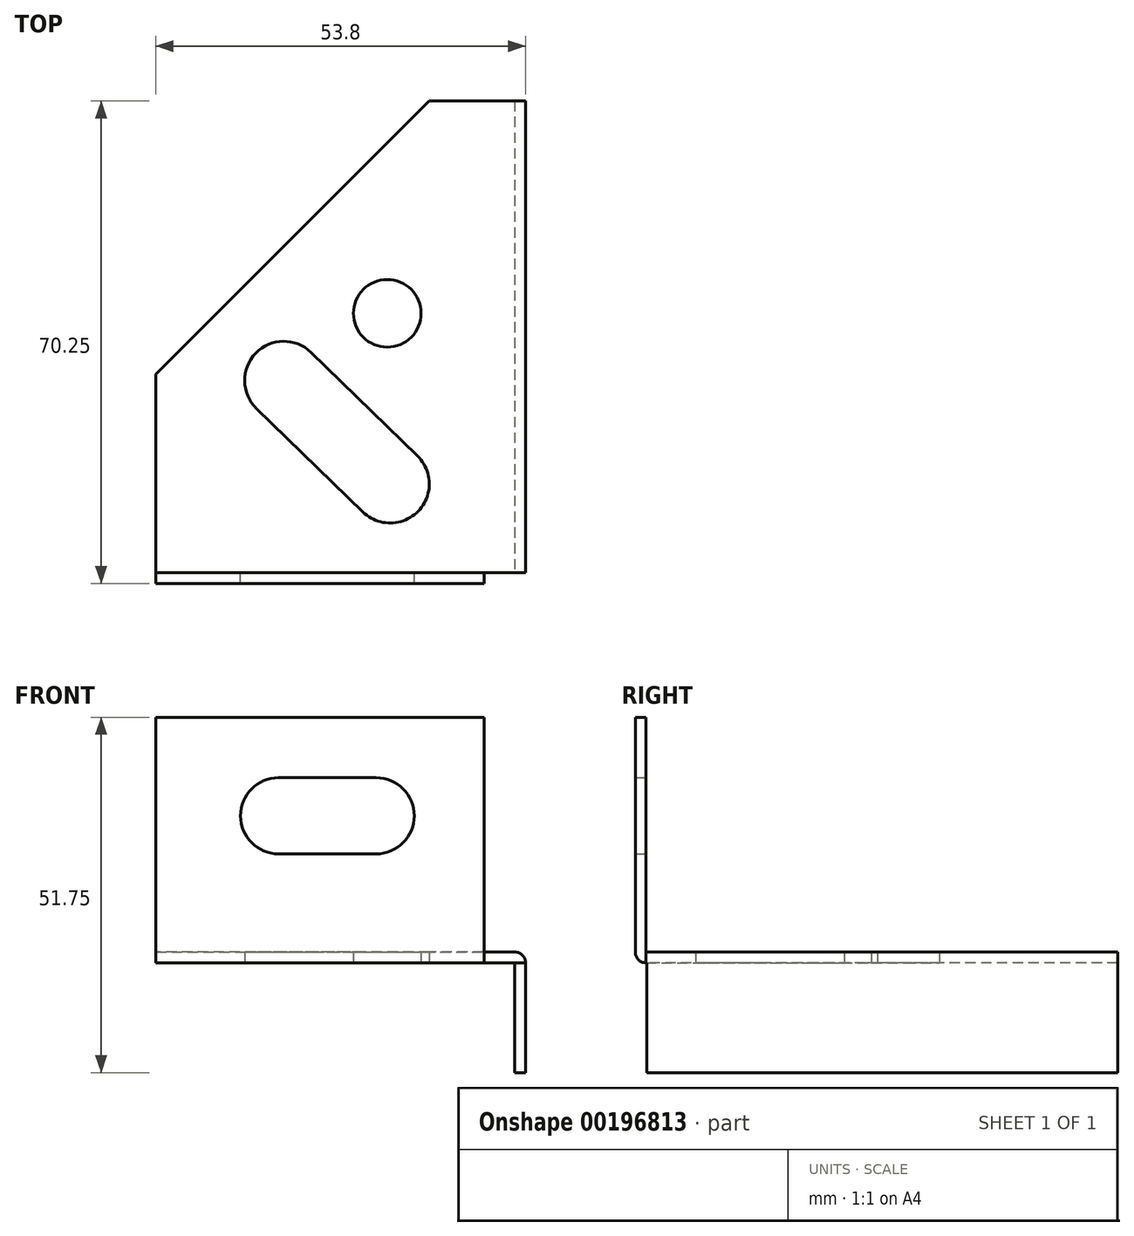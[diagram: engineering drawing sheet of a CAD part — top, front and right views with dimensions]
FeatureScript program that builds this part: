
annotation { "Feature Type Name" : "Feature", "Feature Type Description" : "" }
export const myFeature = defineFeature(function(context is Context, id is Id, definition is map)
    precondition{}
    {
        {
            var Q0;
            Q0=qCreatedBy(makeId("Top.planeOp"),FACE);
            var sketch = newSketch(context, id + "F0", { "sketchPlane" : qUnion([Q0])});
            skLineSegment(sketch, "E0", {"start": v(-51.36, -58.28) * mm, "end": v(2.44, -58.28) * mm});
            skLineSegment(sketch, "E1", {"start": v(2.44, -58.28) * mm, "end": v(2.44, -29.38) * mm});
            skLineSegment(sketch, "E2", {"start": v(-51.36, -58.28) * mm, "end": v(-51.36, 10.42) * mm});
            skLineSegment(sketch, "E3", {"start": v(-51.36, 10.42) * mm, "end": v(-37.36, 10.42) * mm});
            skLineSegment(sketch, "E4", {"start": v(-37.36, 10.42) * mm, "end": v(2.44, -29.38) * mm});
            skCircle(sketch, "E5", {"center": v(-31.23, -20.5) * mm, "radius": 4.92 * mm});
            skCircle(sketch, "E6", {"center": v(-31.66, -45.34) * mm, "radius": 5.7 * mm});
            skCircle(sketch, "E7", {"center": v(-16.17, -30.28) * mm, "radius": 5.7 * mm});
            skLineSegment(sketch, "E8", {"start": v(-20.15, -26.2) * mm, "end": v(-35.63, -41.25) * mm});
            skLineSegment(sketch, "E9", {"start": v(-27.68, -49.42) * mm, "end": v(-12.2, -34.36) * mm});
            skSolve(sketch);
        }
        {
            var Q0;
            Q0=makeQuery(id+"F0.imprint","IMPRINT",FACE,{"disambiguationData":[TD([[makeQuery(id+"F0.imprint","IMPRINT",EDGE,{"derivedFrom":sQuery(id+"F0.wireOp",EDGE,"E0")}),1.0]])]});
            extrude(context, id + "F1", {"entities" : qUnion([Q0]), "depth" : 1.55 * mm});
        }
        {
            var Q0;
            Q0=makeQuery(id+"F1.opExtrude","CAP_FACE",FACE,{"disambiguationData":[OSD([sQuery(id+"F0.wireOp",EDGE,"E0"),sQuery(id+"F0.wireOp",EDGE,"E1"),sQuery(id+"F0.wireOp",EDGE,"E2"),sQuery(id+"F0.wireOp",EDGE,"E3"),sQuery(id+"F0.wireOp",EDGE,"E4"),sQuery(id+"F0.wireOp",EDGE,"E5"),sQuery(id+"F0.wireOp",EDGE,"E6"),sQuery(id+"F0.wireOp",EDGE,"E7"),sQuery(id+"F0.wireOp",EDGE,"E8"),sQuery(id+"F0.wireOp",EDGE,"E9")])],"isStart":true});
            var sketch = newSketch(context, id + "F2", { "sketchPlane" : qUnion([Q0])});
            skLineSegment(sketch, "E10.bottom", {"start": v(-51.36, -10.42) * mm, "end": v(-49.8, -10.42) * mm});
            skLineSegment(sketch, "E10.top", {"start": v(-51.36, 58.18) * mm, "end": v(-49.8, 58.18) * mm});
            skLineSegment(sketch, "E10.left", {"start": v(-51.36, -10.42) * mm, "end": v(-51.36, 58.18) * mm});
            skLineSegment(sketch, "E10.right", {"start": v(-49.8, -10.42) * mm, "end": v(-49.8, 58.18) * mm});
            skSolve(sketch);
        }
        {
            var Q0;
            Q0=makeQuery(id+"F2.imprint","IMPRINT",FACE,{"disambiguationData":[TD([[makeQuery(id+"F2.imprint","IMPRINT",EDGE,{"derivedFrom":sQuery(id+"F2.wireOp",EDGE,"E10.bottom")}),1.0]])]});
            extrude(context, id + "F3", {"entities" : qUnion([Q0]), "operationType" : NewBodyOperationType.ADD, "depth" : 16 * mm});
        }
        {
            var Q0;
            Q0=makeQuery(id+"F1.opExtrude","CAP_FACE",FACE,{"disambiguationData":[OSD([sQuery(id+"F0.wireOp",EDGE,"E0"),sQuery(id+"F0.wireOp",EDGE,"E1"),sQuery(id+"F0.wireOp",EDGE,"E2"),sQuery(id+"F0.wireOp",EDGE,"E3"),sQuery(id+"F0.wireOp",EDGE,"E4"),sQuery(id+"F0.wireOp",EDGE,"E5"),sQuery(id+"F0.wireOp",EDGE,"E6"),sQuery(id+"F0.wireOp",EDGE,"E7"),sQuery(id+"F0.wireOp",EDGE,"E8"),sQuery(id+"F0.wireOp",EDGE,"E9")])],"isStart":false});
            var sketch = newSketch(context, id + "F4", { "sketchPlane" : qUnion([Q0])});
            skLineSegment(sketch, "E11.bottom", {"start": v(2.44, -58.28) * mm, "end": v(-45.36, -58.28) * mm});
            skLineSegment(sketch, "E11.top", {"start": v(2.44, -59.83) * mm, "end": v(-45.36, -59.83) * mm});
            skLineSegment(sketch, "E11.left", {"start": v(2.44, -58.28) * mm, "end": v(2.44, -59.83) * mm});
            skLineSegment(sketch, "E11.right", {"start": v(-45.36, -58.28) * mm, "end": v(-45.36, -59.83) * mm});
            skSolve(sketch);
        }
        {
            var Q0;
            Q0=makeQuery(id+"F4.imprint","IMPRINT",FACE,{"disambiguationData":[TD([[makeQuery(id+"F4.imprint","IMPRINT",EDGE,{"derivedFrom":sQuery(id+"F4.wireOp",EDGE,"E11.bottom")}),-1.0]])]});
            extrude(context, id + "F5", {"entities" : qUnion([Q0]), "operationType" : NewBodyOperationType.ADD, "oppositeDirection" : true, "depth" : 1.55 * mm});
        }
        {
            var Q0;
            Q0=makeQuery(id+"F5.boolean.opBoolean","MERGE",FACE,{"derivedFrom":[makeQuery(id+"F1.opExtrude","CAP_FACE",FACE,{"disambiguationData":[OSD([sQuery(id+"F0.wireOp",EDGE,"E0"),sQuery(id+"F0.wireOp",EDGE,"E1"),sQuery(id+"F0.wireOp",EDGE,"E2"),sQuery(id+"F0.wireOp",EDGE,"E3"),sQuery(id+"F0.wireOp",EDGE,"E4"),sQuery(id+"F0.wireOp",EDGE,"E5"),sQuery(id+"F0.wireOp",EDGE,"E6"),sQuery(id+"F0.wireOp",EDGE,"E7"),sQuery(id+"F0.wireOp",EDGE,"E8"),sQuery(id+"F0.wireOp",EDGE,"E9")])],"isStart":false}),makeQuery(id+"F5.opExtrude","CAP_FACE",FACE,{"disambiguationData":[OSD([sQuery(id+"F4.wireOp",EDGE,"E11.bottom"),sQuery(id+"F4.wireOp",EDGE,"E11.top"),sQuery(id+"F4.wireOp",EDGE,"E11.left"),sQuery(id+"F4.wireOp",EDGE,"E11.right")])],"isStart":true})]});
            var sketch = newSketch(context, id + "F6", { "sketchPlane" : qUnion([Q0])});
            skLineSegment(sketch, "E12.bottom", {"start": v(2.44, -59.83) * mm, "end": v(-45.36, -59.83) * mm});
            skLineSegment(sketch, "E12.top", {"start": v(2.44, -58.28) * mm, "end": v(-45.36, -58.28) * mm});
            skLineSegment(sketch, "E12.left", {"start": v(2.44, -59.83) * mm, "end": v(2.44, -58.28) * mm});
            skLineSegment(sketch, "E12.right", {"start": v(-45.36, -59.83) * mm, "end": v(-45.36, -58.28) * mm});
            skSolve(sketch);
        }
        {
            var Q0;
            Q0=makeQuery(id+"F6.imprint","IMPRINT",FACE,{"disambiguationData":[TD([[makeQuery(id+"F6.imprint","IMPRINT",EDGE,{"derivedFrom":sQuery(id+"F6.wireOp",EDGE,"E12.bottom")}),-1.0]])]});
            extrude(context, id + "F7", {"entities" : qUnion([Q0]), "operationType" : NewBodyOperationType.ADD, "depth" : 34.2 * mm});
        }
        {
            var Q0;
            Q0=makeQuery(id+"F5.opExtrude","CAP_EDGE",EDGE,{"disambiguationData":[OSD([sQuery(id+"F4.wireOp",EDGE,"E11.top")])],"isStart":false});
            var Q1;
            Q1=makeQuery(id+"F1.opExtrude","CAP_EDGE",EDGE,{"disambiguationData":[OSD([sQuery(id+"F0.wireOp",EDGE,"E2")])],"isStart":false});
            fillet(context, id + "F8", {"entities" : qUnion([Q0, Q1]), "radius" : 1.5 * mm, "tangentPropagation" : true, "allowEdgeOverflow" : false});
        }
        {
            var Q0;
            Q0=makeQuery(id+"F1.opExtrude","SWEPT_BODY",BODY,{"disambiguationData":[OSD([sQuery(id+"F0.wireOp",EDGE,"E0"),sQuery(id+"F0.wireOp",EDGE,"E1"),sQuery(id+"F0.wireOp",EDGE,"E2"),sQuery(id+"F0.wireOp",EDGE,"E3"),sQuery(id+"F0.wireOp",EDGE,"E4"),sQuery(id+"F0.wireOp",EDGE,"E5"),sQuery(id+"F0.wireOp",EDGE,"E6"),sQuery(id+"F0.wireOp",EDGE,"E7"),sQuery(id+"F0.wireOp",EDGE,"E8"),sQuery(id+"F0.wireOp",EDGE,"E9")])]});
            var Q1;
            Q1=qCreatedBy(makeId("Right.planeOp"),FACE);
            mirror(context, id + "F9", {"entities" : qUnion([Q0]), "mirrorPlane" : qUnion([Q1])});
        }
        {
            var Q0;
            Q0=makeQuery(id+"F1.opExtrude","SWEPT_BODY",BODY,{"disambiguationData":[OSD([sQuery(id+"F0.wireOp",EDGE,"E0"),sQuery(id+"F0.wireOp",EDGE,"E1"),sQuery(id+"F0.wireOp",EDGE,"E2"),sQuery(id+"F0.wireOp",EDGE,"E3"),sQuery(id+"F0.wireOp",EDGE,"E4"),sQuery(id+"F0.wireOp",EDGE,"E5"),sQuery(id+"F0.wireOp",EDGE,"E6"),sQuery(id+"F0.wireOp",EDGE,"E7"),sQuery(id+"F0.wireOp",EDGE,"E8"),sQuery(id+"F0.wireOp",EDGE,"E9")])]});
            deleteBodies(context, id + "F10", {"entities" : qUnion([Q0])});
        }
        {
            var Q0;
            Q0=makeQuery(id+"F9.opPattern","COPY",FACE,{"derivedFrom":makeQuery(id+"F7.opExtrude","SWEPT_FACE",FACE,{"disambiguationData":[OSD([sQuery(id+"F6.wireOp",EDGE,"E12.top")])]}),"instanceName":"1"});
            var sketch = newSketch(context, id + "F11", { "sketchPlane" : qUnion([Q0])});
            skCircle(sketch, "E13", {"center": v(-29.6, 21.4) * mm, "radius": 5.55 * mm});
            skCircle(sketch, "E14", {"center": v(-15.4, 21.4) * mm, "radius": 5.55 * mm});
            skLineSegment(sketch, "E15", {"start": v(-29.6, 26.95) * mm, "end": v(-15.4, 26.95) * mm});
            skLineSegment(sketch, "E16", {"start": v(-29.6, 15.85) * mm, "end": v(-15.4, 15.85) * mm});
            skSolve(sketch);
        }
        {
            var Q0;
            {var subQ0=sQuery(id+"F11.wireOp",EDGE,"E13");var subQ1=makeQuery(id+"F11.imprint","INTERSECT",VERTEX,{"derivedFrom":[subQ0,sQuery(id+"F11.wireOp",EDGE,"E15")]});Q0=makeQuery(id+"F11.imprint","IMPRINT",FACE,{"disambiguationData":[TD([[makeQuery(id+"F11.imprint","IMPRINT",EDGE,{"disambiguationData":[TD([[subQ1,-1.0]])],"derivedFrom":subQ0}),1.0]])]});}
            var Q1;
            {var subQ0=sQuery(id+"F11.wireOp",EDGE,"E15");Q1=makeQuery(id+"F11.imprint","IMPRINT",FACE,{"disambiguationData":[TD([[makeQuery(id+"F11.imprint","IMPRINT",EDGE,{"derivedFrom":subQ0}),-1.0]])]});}
            var Q2;
            {var subQ0=sQuery(id+"F11.wireOp",EDGE,"E14");var subQ1=makeQuery(id+"F11.imprint","INTERSECT",VERTEX,{"derivedFrom":[subQ0,sQuery(id+"F11.wireOp",EDGE,"E15")]});Q2=makeQuery(id+"F11.imprint","IMPRINT",FACE,{"disambiguationData":[TD([[makeQuery(id+"F11.imprint","IMPRINT",EDGE,{"disambiguationData":[TD([[subQ1,-1.0]])],"derivedFrom":subQ0}),1.0]])]});}
            extrude(context, id + "F12", {"entities" : qUnion([Q0, Q1, Q2]), "operationType" : NewBodyOperationType.REMOVE, "endBound" : BoundingType.THROUGH_ALL, "oppositeDirection" : true, "depth" : 25 * mm});
        }
    });
